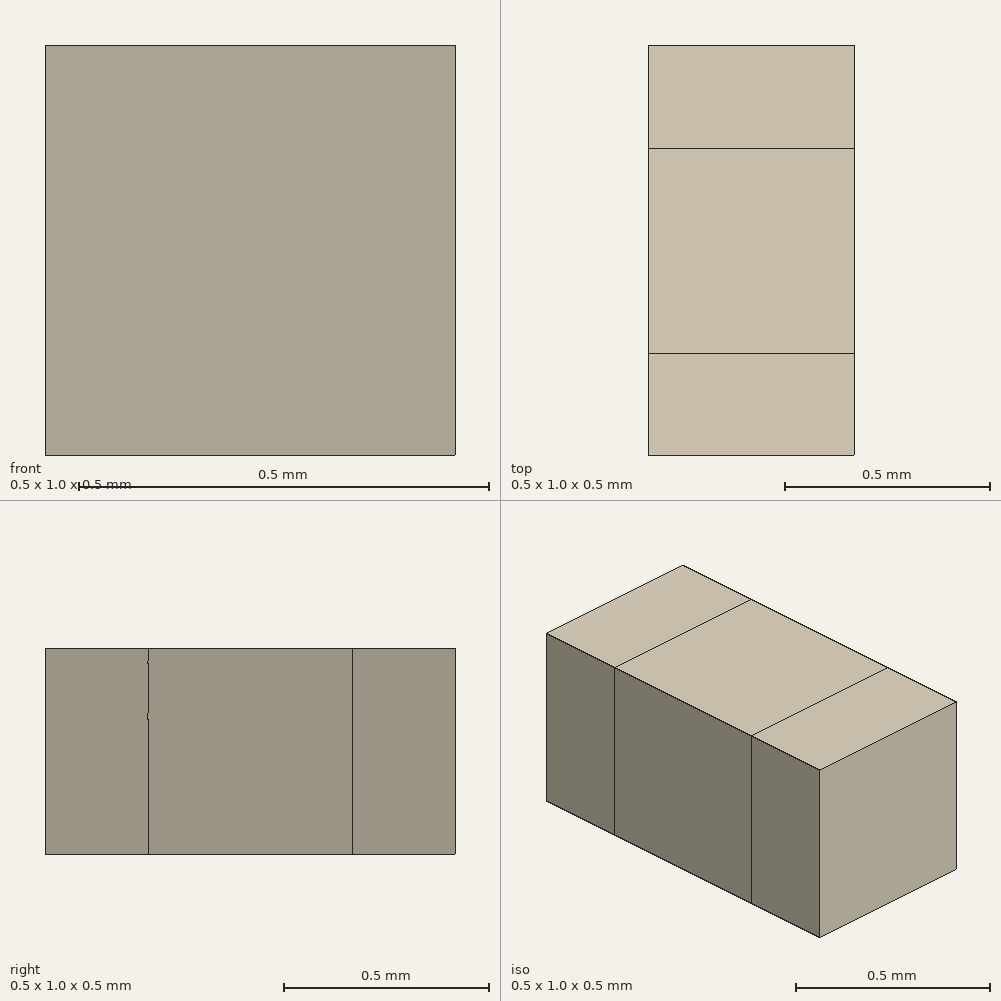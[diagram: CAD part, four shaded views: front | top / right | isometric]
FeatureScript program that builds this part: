
annotation { "Feature Type Name" : "Feature", "Feature Type Description" : "" }
export const myFeature = defineFeature(function(context is Context, id is Id, definition is map)
    precondition{}
    {
        {
            var Q0;
            Q0=qCreatedBy(makeId("Top.planeOp"),FACE);
            var sketch = newSketch(context, id + "F0", { "sketchPlane" : qUnion([Q0])});
            skLineSegment(sketch, "E0.bottom", {"start": v(-0.25, 0.5) * mm, "end": v(0.25, 0.5) * mm});
            skLineSegment(sketch, "E0.top", {"start": v(-0.25, -0.5) * mm, "end": v(0.25, -0.5) * mm});
            skLineSegment(sketch, "E0.left", {"start": v(-0.25, 0.5) * mm, "end": v(-0.25, -0.5) * mm});
            skLineSegment(sketch, "E0.right", {"start": v(0.25, 0.5) * mm, "end": v(0.25, -0.5) * mm});
            skPoint(sketch, "E0.middle", {"position": v(0, 0) * mm});
            skLineSegment(sketch, "E1", {"start": v(-0.25, 0.25) * mm, "end": v(0.25, 0.25) * mm});
            skLineSegment(sketch, "E2", {"start": v(-0.25, -0.25) * mm, "end": v(0.25, -0.25) * mm});
            skSolve(sketch);
        }
        {
            var Q0;
            {var subQ0=sQuery(id+"F0.wireOp",EDGE,"E0.top");Q0=makeQuery(id+"F0.imprint","IMPRINT",FACE,{"disambiguationData":[TD([[makeQuery(id+"F0.imprint","IMPRINT",EDGE,{"derivedFrom":subQ0}),1.0]])]});}
            extrude(context, id + "F1", {"entities" : qUnion([Q0]), "depth" : 0.5 * mm});
        }
        {
            var Q0;
            {var subQ0=sQuery(id+"F0.wireOp",EDGE,"E0.bottom");Q0=makeQuery(id+"F0.imprint","IMPRINT",FACE,{"disambiguationData":[TD([[makeQuery(id+"F0.imprint","IMPRINT",EDGE,{"derivedFrom":subQ0}),-1.0]])]});}
            extrude(context, id + "F2", {"entities" : qUnion([Q0]), "depth" : 0.5 * mm});
        }
        {
            var Q0;
            {var subQ0=sQuery(id+"F0.wireOp",EDGE,"E1");Q0=makeQuery(id+"F0.imprint","IMPRINT",FACE,{"disambiguationData":[TD([[makeQuery(id+"F0.imprint","IMPRINT",EDGE,{"derivedFrom":subQ0}),-1.0]])]});}
            extrude(context, id + "F3", {"entities" : qUnion([Q0]), "depth" : 0.5 * mm});
        }
    });
